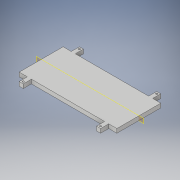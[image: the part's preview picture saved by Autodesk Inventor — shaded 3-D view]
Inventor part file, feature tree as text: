
AUTODESK INVENTOR PART (.ipt)
format: ipt  version: 2018 (Build 220112000, 112)  size: 138,240 bytes
history: native  units: in
note: dims shown in document units (in); Inventor stores cm internally (conversion verified against a paired STEP export)
features: extrude x2, sketch x2, plane x1, mirror x1
ambient origin geometry x8: Origin, YZ Plane, XZ Plane, XY Plane, X Axis, Y Axis, Z Axis, Center Point
bodies: Solid1 (feature_tree)
feature tree (6):
  extrude  "Extrusion1"  Depth=2.7in
  extrude  "Extrusion2"  TaperAngle=0.0deg  [1 undecoded]
  plane  "Work Plane1"
  mirror  "Mirror1"
  sketch  "Sketch1"  dims[d0=6.0in d1=2.7in]
  sketch  "Sketch2"  dims[d2=0.25in d3=0.0in d4=0.5in d5=0.25in d6=0.11in d7=0.125in d8=0.125in d9=0.0in d10=0.5in d11=0.5in d12=0.25in d13=0.11in d14=0.125in d15=0.125in d16=0.0in d17=0.5in d18=0.25in d19=0.0in]
note: 1 required parameter value undecoded (feature->parameter linkage not recoverable at this tier; creation-order binding heuristic only, values carry confidence <= 0.55)
